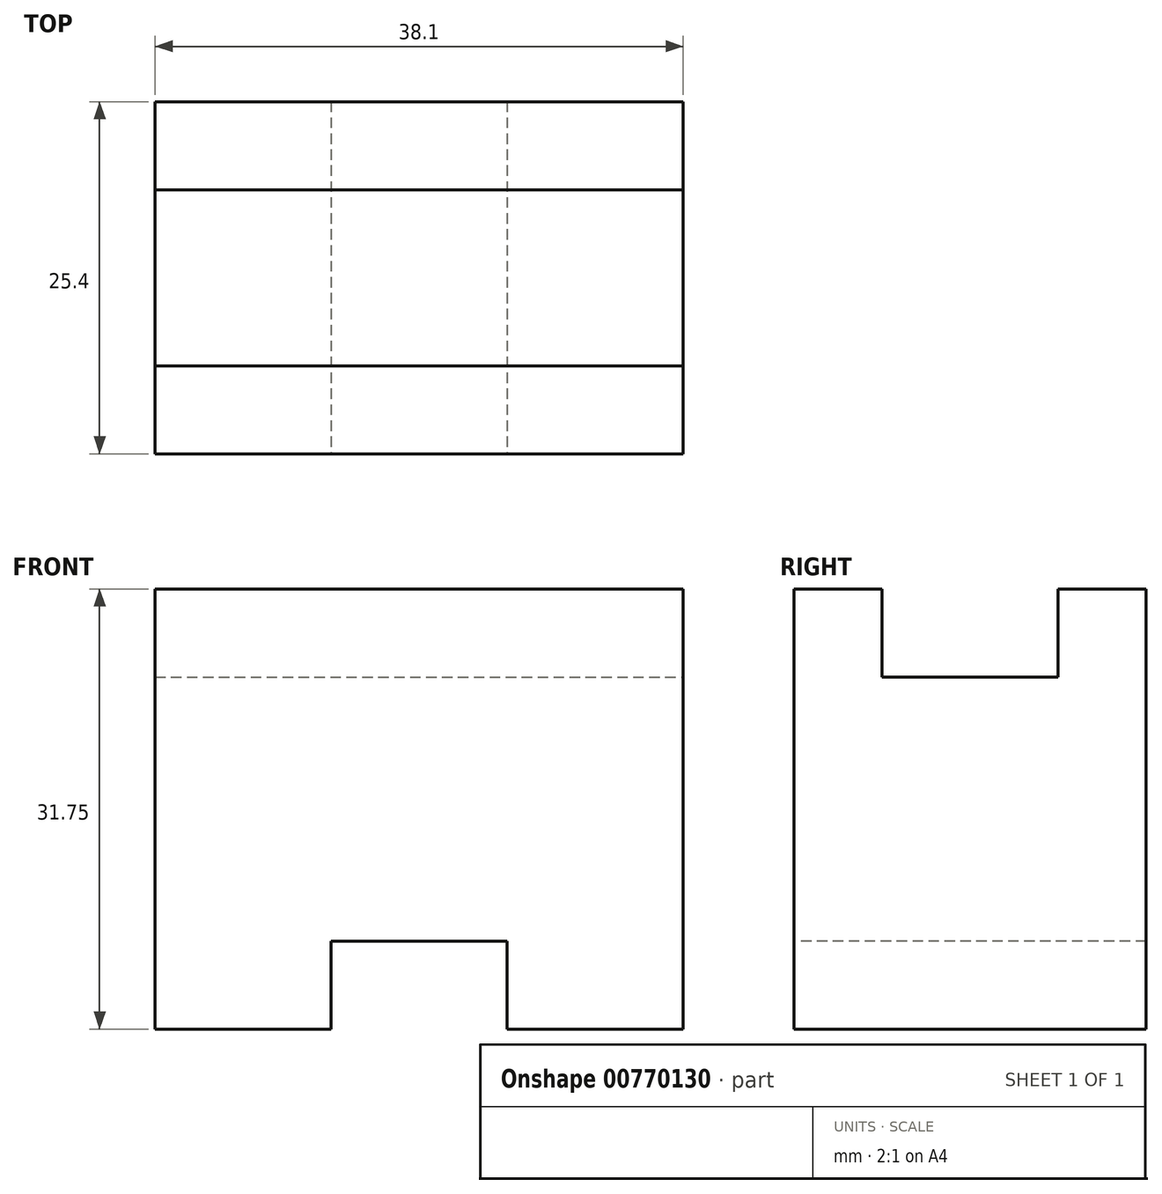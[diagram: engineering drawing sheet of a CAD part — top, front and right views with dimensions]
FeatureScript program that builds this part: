
annotation { "Feature Type Name" : "Feature", "Feature Type Description" : "" }
export const myFeature = defineFeature(function(context is Context, id is Id, definition is map)
    precondition{}
    {
        {
            var Q0;
            Q0=qCreatedBy(makeId("Front.planeOp"),FACE);
            var sketch = newSketch(context, id + "F0", { "sketchPlane" : qUnion([Q0])});
            skLineSegment(sketch, "E0", {"start": v(0, 0) * mm, "end": v(38.1, 0) * mm});
            skLineSegment(sketch, "E1", {"start": v(38.1, 0) * mm, "end": v(38.1, 31.75) * mm});
            skLineSegment(sketch, "E2", {"start": v(38.1, 31.75) * mm, "end": v(0, 31.75) * mm});
            skLineSegment(sketch, "E3", {"start": v(0, 31.75) * mm, "end": v(0, 0) * mm});
            skSolve(sketch);
        }
        {
            var Q0;
            Q0 = qSketchRegion(id + "F0", true);
            extrude(context, id + "F1", {"entities" : qUnion([Q0]), "depth" : 25.4 * mm, "offsetDistance" : 25.4 * mm});
        }
        {
            var Q0;
            Q0=makeQuery(id+"F1.opExtrude","SWEPT_FACE",FACE,{"disambiguationData":[OSD([sQuery(id+"F0.wireOp",EDGE,"E2")])]});
            var sketch = newSketch(context, id + "F2", { "sketchPlane" : qUnion([Q0])});
            skLineSegment(sketch, "E4", {"start": v(0, -6.35) * mm, "end": v(38.1, -6.35) * mm});
            skLineSegment(sketch, "E5", {"start": v(38.1, -6.35) * mm, "end": v(38.1, -19.05) * mm});
            skLineSegment(sketch, "E6", {"start": v(38.1, -19.05) * mm, "end": v(0, -19.05) * mm});
            skLineSegment(sketch, "E7", {"start": v(0, -19.05) * mm, "end": v(0, -6.35) * mm});
            skSolve(sketch);
        }
        {
            var Q0;
            Q0=makeQuery(id+"F2.imprint","IMPRINT",FACE,{"disambiguationData":[TD([[makeQuery(id+"F2.imprint","IMPRINT",EDGE,{"derivedFrom":sQuery(id+"F2.wireOp",EDGE,"E4")}),-1.0]])]});
            extrude(context, id + "F3", {"entities" : qUnion([Q0]), "operationType" : NewBodyOperationType.REMOVE, "oppositeDirection" : true, "depth" : 6.35 * mm, "offsetDistance" : 25.4 * mm});
        }
        {
            var Q0;
            Q0=makeQuery(id+"F1.opExtrude","CAP_FACE",FACE,{"disambiguationData":[OSD([sQuery(id+"F0.wireOp",EDGE,"E0"),sQuery(id+"F0.wireOp",EDGE,"E1"),sQuery(id+"F0.wireOp",EDGE,"E2"),sQuery(id+"F0.wireOp",EDGE,"E3")])],"isStart":false});
            var sketch = newSketch(context, id + "F4", { "sketchPlane" : qUnion([Q0])});
            skLineSegment(sketch, "E8", {"start": v(12.7, 0) * mm, "end": v(12.7, 6.35) * mm});
            skLineSegment(sketch, "E9", {"start": v(12.7, 6.35) * mm, "end": v(25.4, 6.35) * mm});
            skLineSegment(sketch, "E10", {"start": v(25.4, 6.35) * mm, "end": v(25.4, 0) * mm});
            skLineSegment(sketch, "E11", {"start": v(25.4, 0) * mm, "end": v(12.7, 0) * mm});
            skSolve(sketch);
        }
        {
            var Q0;
            Q0=makeQuery(id+"F4.imprint","IMPRINT",FACE,{"disambiguationData":[TD([[makeQuery(id+"F4.imprint","IMPRINT",EDGE,{"derivedFrom":sQuery(id+"F4.wireOp",EDGE,"E8")}),-1.0]])]});
            extrude(context, id + "F5", {"entities" : qUnion([Q0]), "operationType" : NewBodyOperationType.REMOVE, "oppositeDirection" : true, "depth" : 25.4 * mm, "offsetDistance" : 25.4 * mm});
        }
    });
